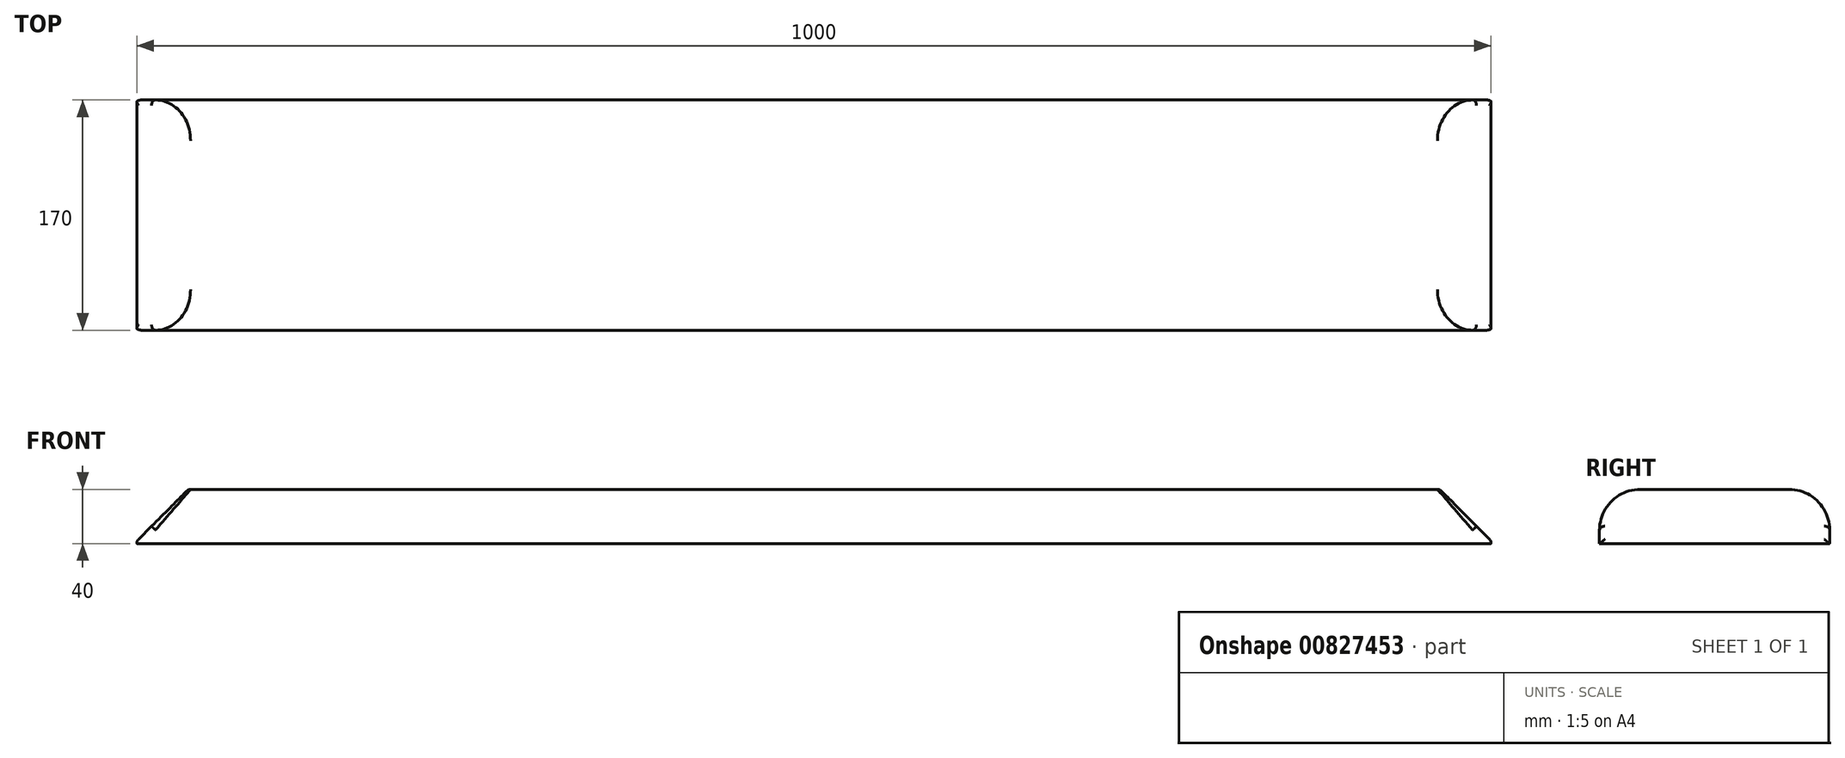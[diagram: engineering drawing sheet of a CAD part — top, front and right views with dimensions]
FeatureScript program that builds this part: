
annotation { "Feature Type Name" : "Feature", "Feature Type Description" : "" }
export const myFeature = defineFeature(function(context is Context, id is Id, definition is map)
    precondition{}
    {
        {
            var Q0;
            Q0=qCreatedBy(makeId("Top.planeOp"),FACE);
            var sketch = newSketch(context, id + "F0", { "sketchPlane" : qUnion([Q0])});
            skLineSegment(sketch, "E0.bottom", {"start": v(500, 85) * mm, "end": v(-500, 85) * mm});
            skLineSegment(sketch, "E0.top", {"start": v(500, -85) * mm, "end": v(-500, -85) * mm});
            skLineSegment(sketch, "E0.left", {"start": v(500, 85) * mm, "end": v(500, -85) * mm});
            skLineSegment(sketch, "E0.right", {"start": v(-500, 85) * mm, "end": v(-500, -85) * mm});
            skPoint(sketch, "E0.middle", {"position": v(0, 0) * mm});
            skPoint(sketch, "E1.center.orphan", {"position": v(0, 66.25) * mm});
            skSolve(sketch);
        }
        {
            var Q0;
            Q0=makeQuery(id+"F0.imprint","IMPRINT",FACE,{"disambiguationData":[TD([[makeQuery(id+"F0.imprint","IMPRINT",EDGE,{"derivedFrom":sQuery(id+"F0.wireOp",EDGE,"E0.bottom")}),1.0]])]});
            extrude(context, id + "F1", {"entities" : qUnion([Q0]), "depth" : 40 * mm, "offsetDistance" : 25 * mm});
        }
        {
            var Q0;
            Q0=makeQuery(id+"F1.opExtrude","SWEPT_FACE",FACE,{"disambiguationData":[OSD([sQuery(id+"F0.wireOp",EDGE,"E0.top")])]});
            var sketch = newSketch(context, id + "F2", { "sketchPlane" : qUnion([Q0])});
            skLineSegment(sketch, "E2", {"start": v(500, 0) * mm, "end": v(500, 2) * mm});
            skLineSegment(sketch, "E3", {"start": v(500, 2) * mm, "end": v(462, 40) * mm});
            skLineSegment(sketch, "E4", {"start": v(462, 40) * mm, "end": v(500, 40) * mm});
            skLineSegment(sketch, "E5", {"start": v(500, 40) * mm, "end": v(500, 2) * mm});
            skLineSegment(sketch, "E6", {"start": v(-500, 0) * mm, "end": v(-500, 2) * mm});
            skLineSegment(sketch, "E7", {"start": v(-500, 2) * mm, "end": v(-462, 40) * mm});
            skLineSegment(sketch, "E8", {"start": v(-462, 40) * mm, "end": v(-500, 40) * mm});
            skLineSegment(sketch, "E9", {"start": v(-500, 40) * mm, "end": v(-500, 2) * mm});
            skSolve(sketch);
        }
        {
            var Q0;
            Q0 = qSketchRegion(id + "F2", true);
            extrude(context, id + "F3", {"entities" : qUnion([Q0]), "operationType" : NewBodyOperationType.REMOVE, "oppositeDirection" : true, "depth" : 170 * mm, "offsetDistance" : 25 * mm});
        }
        {
            var Q0;
            Q0=makeQuery(id+"F1.opExtrude","CAP_EDGE",EDGE,{"disambiguationData":[OSD([sQuery(id+"F0.wireOp",EDGE,"E0.top")])],"isStart":false});
            var Q1;
            Q1=makeQuery(id+"F1.opExtrude","CAP_EDGE",EDGE,{"disambiguationData":[OSD([sQuery(id+"F0.wireOp",EDGE,"E0.bottom")])],"isStart":false});
            fillet(context, id + "F4", {"entities" : qUnion([Q0, Q1]), "radius" : 30 * mm, "tangentPropagation" : true, "allowEdgeOverflow" : false});
        }
        {
            var Q0;
            Q0=makeQuery(id+"F3.boolean.opBoolean","COPY",EDGE,{"derivedFrom":makeQuery(id+"F3.opExtrude","SWEPT_EDGE",EDGE,{"disambiguationData":[OSD([sQuery(id+"F0.wireOp",EDGE,"E0.top"),sQuery(id+"F2.wireOp",EDGE,"E3"),sQuery(id+"F2.wireOp",EDGE,"E4")])]})});
            var Q1;
            Q1=makeQuery(id+"F3.boolean.opBoolean","COPY",FACE,{"derivedFrom":makeQuery(id+"F3.opExtrude","SWEPT_FACE",FACE,{"disambiguationData":[OSD([sQuery(id+"F2.wireOp",EDGE,"E3")])]})});
            fillet(context, id + "F5", {"entities" : qUnion([Q0, Q1]), "radius" : 4 * mm, "tangentPropagation" : true, "allowEdgeOverflow" : false});
        }
        {
            var Q0;
            Q0=makeQuery(id+"F3.boolean.opBoolean","COPY",FACE,{"derivedFrom":makeQuery(id+"F3.opExtrude","SWEPT_FACE",FACE,{"disambiguationData":[OSD([sQuery(id+"F2.wireOp",EDGE,"E7")])]})});
            fillet(context, id + "F6", {"entities" : qUnion([Q0]), "radius" : 4 * mm, "tangentPropagation" : true, "allowEdgeOverflow" : false});
        }
    });
